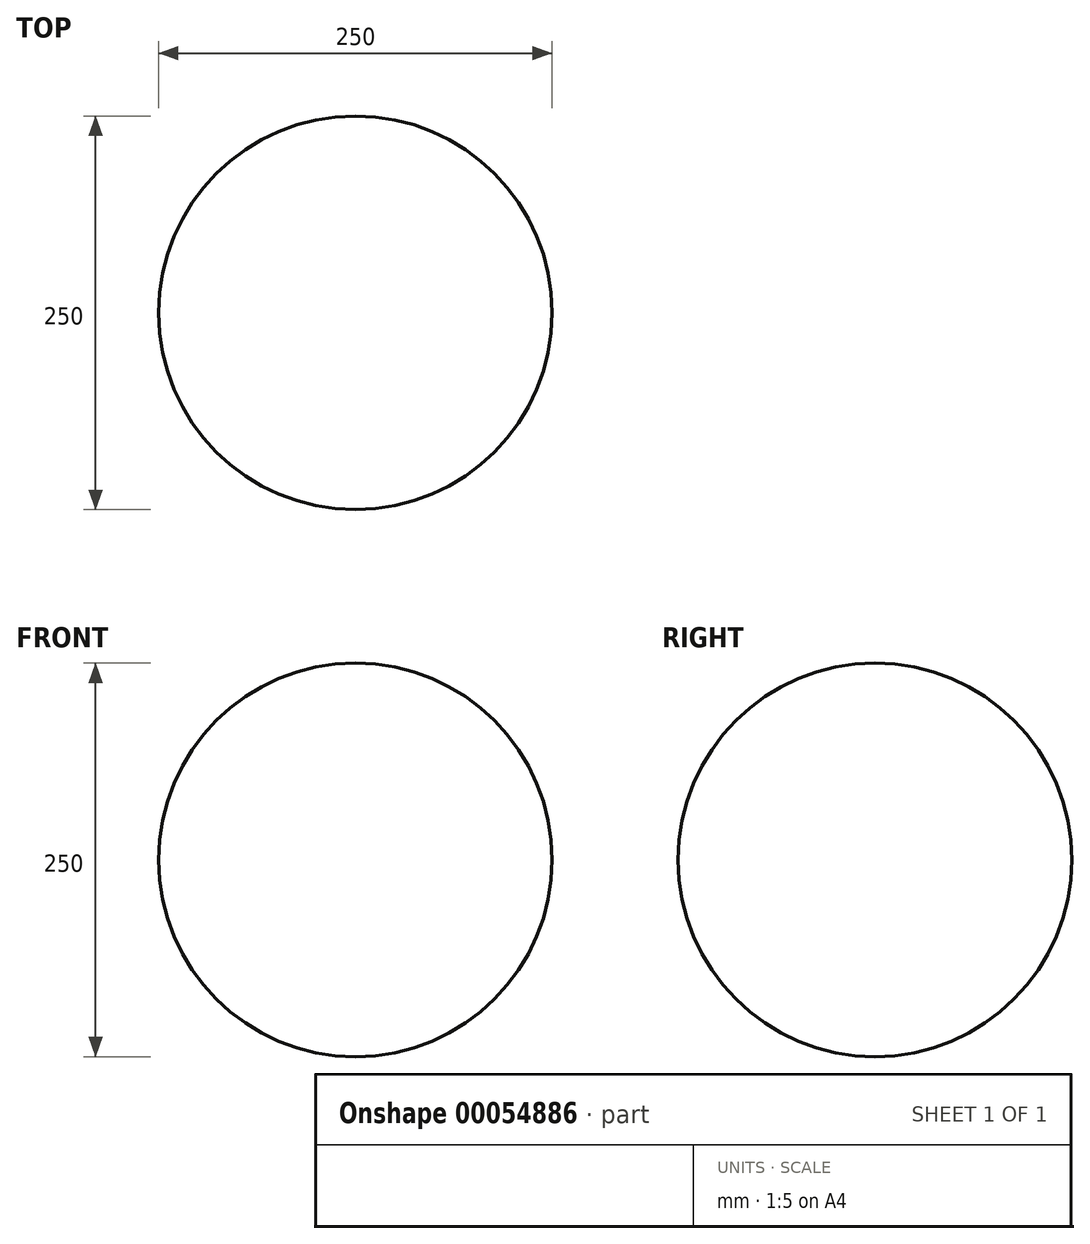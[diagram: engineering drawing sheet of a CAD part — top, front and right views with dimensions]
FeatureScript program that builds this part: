
annotation { "Feature Type Name" : "Feature", "Feature Type Description" : "" }
export const myFeature = defineFeature(function(context is Context, id is Id, definition is map)
    precondition{}
    {
        {
            var Q0;
            Q0=qCreatedBy(makeId("Front.planeOp"),FACE);
            var sketch = newSketch(context, id + "F0", { "sketchPlane" : qUnion([Q0])});
            skArc(sketch, "E0", {"start": v(0, -125) * mm, "mid": v(125, 0) * mm, "end": v(0, 125) * mm});
            skLineSegment(sketch, "E1", {"start": v(0, 125) * mm, "end": v(0, -125) * mm});
            skLineSegment(sketch, "E2", {"start": v(0, 125) * mm, "end": v(0, 159.1) * mm, "construction": true});
            skSolve(sketch);
        }
        {
            var Q0;
            Q0 = qSketchRegion(id + "F0", true);
            var Q1;
            Q1=sQuery(id+"F0.wireOp",EDGE,"E2");
            revolve(context, id + "F1", {"entities" : qUnion([Q0]), "axis" : qUnion([Q1]), "revolveType" : RevolveType.FULL});
        }
    });
